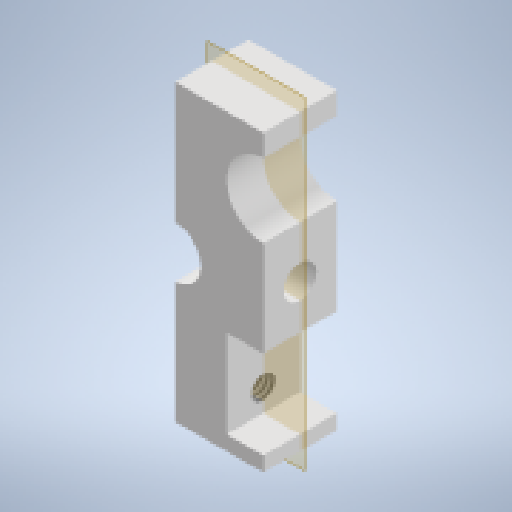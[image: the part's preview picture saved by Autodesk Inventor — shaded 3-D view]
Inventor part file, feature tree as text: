
AUTODESK INVENTOR PART (.ipt)
format: ipt  version: 2023 (Build 270158000, 158)  size: 233,472 bytes
history: native  units: mm
features: extrude x7, sketch x7, thread x2, plane x1
ambient origin geometry x8: Origin, YZ Plane, XZ Plane, XY Plane, X Axis, Y Axis, Z Axis, Center Point
bodies: Solid1 (feature_tree)
feature tree (17):
  extrude  "Extrusion1"  Depth=20.0mm
  plane  "Work Plane1"
  extrude  "Extrusion2"  Depth=2.0mm
  extrude  "Extrusion3"  Depth=4.0mm
  extrude  "Extrusion4"  Depth=5.0mm TaperAngle=0.0deg
  thread  "Thread1"  [1 undecoded]
  thread  "Thread2"  [1 undecoded]
  extrude  "Extrusion5"  Depth=8.0mm TaperAngle=0.0deg
  extrude  "Extrusion6"  Depth=1.6mm
  extrude  "Extrusion7"  Depth=10.0mm
  sketch  "Sketch1"  dims[d0=20.0mm d1=20.0mm]
  sketch  "Sketch2"  dims[d2=4.0mm d6=2.0mm]
  sketch  "Sketch3"  dims[d7=2.0mm d8=4.0mm]
  sketch  "Sketch4"  dims[d9=2.0mm d10=5.0mm d11=0.0mm d12=5.5mm d13=1.8mm d14=0.0mm]
  sketch  "Sketch5"  dims[d15=3.5mm d16=8.0mm d17=0.0mm]
  sketch  "Sketch6"  dims[d18=1.6mm d19=1.6mm]
  sketch  "Sketch7"  dims[d20=2.5mm d21=2.5mm d22=2.5mm d23=2.5mm d24=5.0mm d25=0.0mm d26=5.0mm d27=0.0mm d28=5.0mm d29=0.0mm d30=5.0mm d31=0.0mm d32=2.5mm d33=1.0mm d34=6.0mm d35=5.0mm d36=4.0mm d37=5.0mm d38=0.0mm d39=2.5mm d40=10.0mm d41=2.2mm d42=20.0mm d43=0.0mm]
note: 2 required parameter values undecoded (feature->parameter linkage not recoverable at this tier; creation-order binding heuristic only, values carry confidence <= 0.55)
